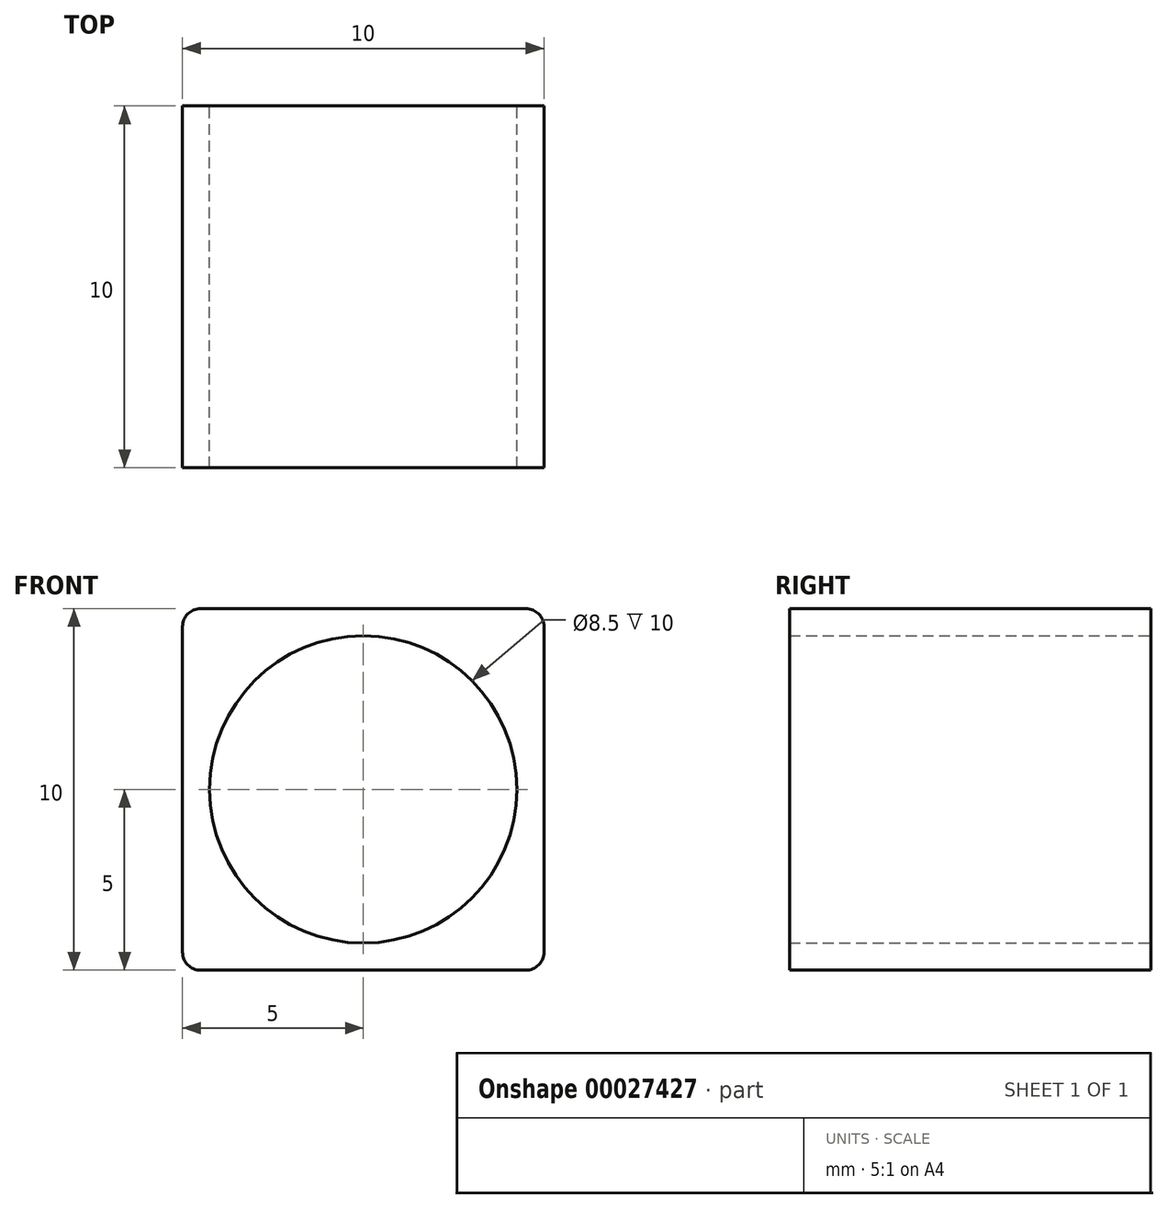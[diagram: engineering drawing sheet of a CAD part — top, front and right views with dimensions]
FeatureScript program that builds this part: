
annotation { "Feature Type Name" : "Feature", "Feature Type Description" : "" }
export const myFeature = defineFeature(function(context is Context, id is Id, definition is map)
    precondition{}
    {
        {
            var Q0;
            Q0=qCreatedBy(makeId("Front.planeOp"),FACE);
            var sketch = newSketch(context, id + "F0", { "sketchPlane" : qUnion([Q0])});
            skCircle(sketch, "E0", {"center": v(0, 0) * mm, "radius": 4.25 * mm});
            skLineSegment(sketch, "E1.rect.bottom", {"start": v(4.5, 5) * mm, "end": v(-4.5, 5) * mm});
            skLineSegment(sketch, "E1.rect.top", {"start": v(4.5, -5) * mm, "end": v(-4.5, -5) * mm});
            skLineSegment(sketch, "E1.rect.left", {"start": v(5, 4.5) * mm, "end": v(5, -4.5) * mm});
            skLineSegment(sketch, "E1.rect.right", {"start": v(-5, 4.5) * mm, "end": v(-5, -4.5) * mm});
            skPoint(sketch, "E2.visualSharp", {"position": v(-5, 5) * mm});
            skArc(sketch, "E2.filletArc", {"start": v(-4.5, 5) * mm, "mid": v(-4.85, 4.85) * mm, "end": v(-5, 4.5) * mm});
            skPoint(sketch, "E3.visualSharp", {"position": v(5, 5) * mm});
            skArc(sketch, "E3.filletArc", {"start": v(5, 4.5) * mm, "mid": v(4.85, 4.85) * mm, "end": v(4.5, 5) * mm});
            skPoint(sketch, "E4.visualSharp", {"position": v(5, -5) * mm});
            skArc(sketch, "E4.filletArc", {"start": v(4.5, -5) * mm, "mid": v(4.85, -4.85) * mm, "end": v(5, -4.5) * mm});
            skPoint(sketch, "E5.visualSharp", {"position": v(-5, -5) * mm});
            skArc(sketch, "E5.filletArc", {"start": v(-5, -4.5) * mm, "mid": v(-4.85, -4.85) * mm, "end": v(-4.5, -5) * mm});
            skSolve(sketch);
        }
        {
            var Q0;
            Q0=makeQuery(id+"F0.imprint","IMPRINT",FACE,{"disambiguationData":[TD([[makeQuery(id+"F0.imprint","IMPRINT",EDGE,{"derivedFrom":sQuery(id+"F0.wireOp",EDGE,"E0")}),-1.0]])]});
            extrude(context, id + "F1", {"entities" : qUnion([Q0]), "depth" : 10 * mm});
        }
    });
